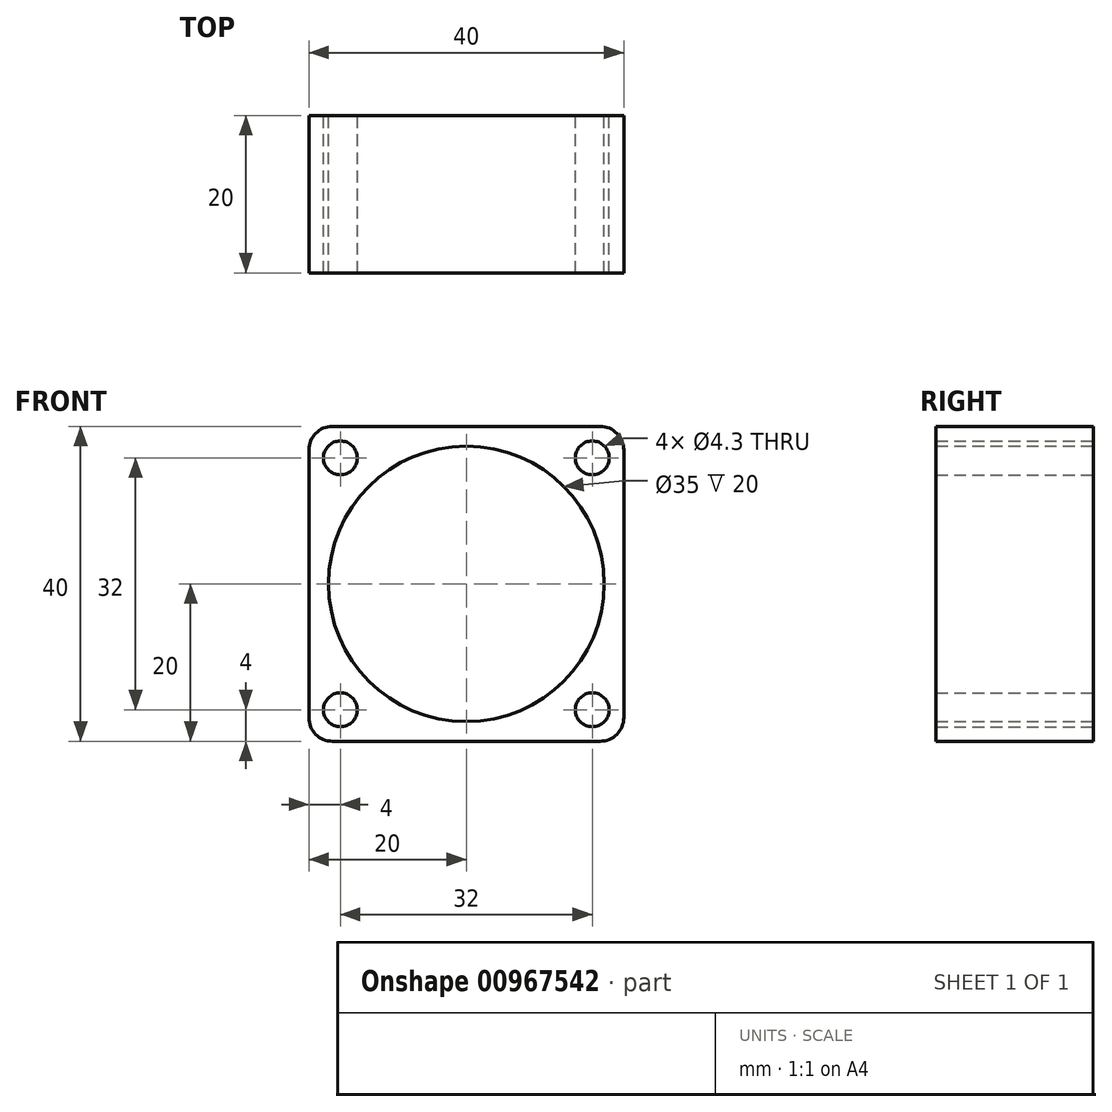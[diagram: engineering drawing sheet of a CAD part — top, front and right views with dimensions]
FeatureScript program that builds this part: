
annotation { "Feature Type Name" : "Feature", "Feature Type Description" : "" }
export const myFeature = defineFeature(function(context is Context, id is Id, definition is map)
    precondition{}
    {
        {
            var Q0;
            Q0=qCreatedBy(makeId("Front.planeOp"),FACE);
            var sketch = newSketch(context, id + "F0", { "sketchPlane" : qUnion([Q0])});
            skLineSegment(sketch, "E0.bottom", {"start": v(-20, 20) * mm, "end": v(20, 20) * mm});
            skLineSegment(sketch, "E0.top", {"start": v(-20, -20) * mm, "end": v(20, -20) * mm});
            skLineSegment(sketch, "E0.left", {"start": v(-20, 20) * mm, "end": v(-20, -20) * mm});
            skLineSegment(sketch, "E0.right", {"start": v(20, 20) * mm, "end": v(20, -20) * mm});
            skPoint(sketch, "E0.middle", {"position": v(0, 0) * mm});
            skLineSegment(sketch, "E1", {"start": v(-20, 20) * mm, "end": v(20, -20) * mm, "construction": true});
            skLineSegment(sketch, "E2", {"start": v(20, 20) * mm, "end": v(-20, -20) * mm, "construction": true});
            skCircle(sketch, "E3", {"center": v(-16, 16) * mm, "radius": 2.15 * mm});
            skCircle(sketch, "E4", {"center": v(16, 16) * mm, "radius": 2.15 * mm});
            skCircle(sketch, "E5", {"center": v(16, -16) * mm, "radius": 2.15 * mm});
            skCircle(sketch, "E6", {"center": v(-16, -16) * mm, "radius": 2.15 * mm});
            skCircle(sketch, "E7", {"center": v(0, 0) * mm, "radius": 17.5 * mm});
            skSolve(sketch);
        }
        {
            var Q0;
            Q0=makeQuery(id+"F0.imprint","IMPRINT",FACE,{"disambiguationData":[TD([[makeQuery(id+"F0.imprint","IMPRINT",EDGE,{"derivedFrom":sQuery(id+"F0.wireOp",EDGE,"E0.bottom")}),-1.0]])]});
            extrude(context, id + "F1", {"entities" : qUnion([Q0]), "depth" : 20 * mm, "offsetDistance" : 25 * mm});
        }
        {
            var Q0;
            Q0=makeQuery(id+"F1.opExtrude","SWEPT_EDGE",EDGE,{"disambiguationData":[OSD([sQuery(id+"F0.wireOp",EDGE,"E0.bottom"),sQuery(id+"F0.wireOp",EDGE,"E0.left")])]});
            var Q1;
            Q1=makeQuery(id+"F1.opExtrude","SWEPT_EDGE",EDGE,{"disambiguationData":[OSD([sQuery(id+"F0.wireOp",EDGE,"E0.bottom"),sQuery(id+"F0.wireOp",EDGE,"E0.right")])]});
            var Q2;
            Q2=makeQuery(id+"F1.opExtrude","SWEPT_EDGE",EDGE,{"disambiguationData":[OSD([sQuery(id+"F0.wireOp",EDGE,"E0.top"),sQuery(id+"F0.wireOp",EDGE,"E0.right")])]});
            var Q3;
            Q3=makeQuery(id+"F1.opExtrude","SWEPT_EDGE",EDGE,{"disambiguationData":[OSD([sQuery(id+"F0.wireOp",EDGE,"E0.top"),sQuery(id+"F0.wireOp",EDGE,"E0.left")])]});
            fillet(context, id + "F2", {"entities" : qUnion([Q0, Q1, Q2, Q3]), "radius" : 3 * mm, "tangentPropagation" : true, "allowEdgeOverflow" : false});
        }
    });
